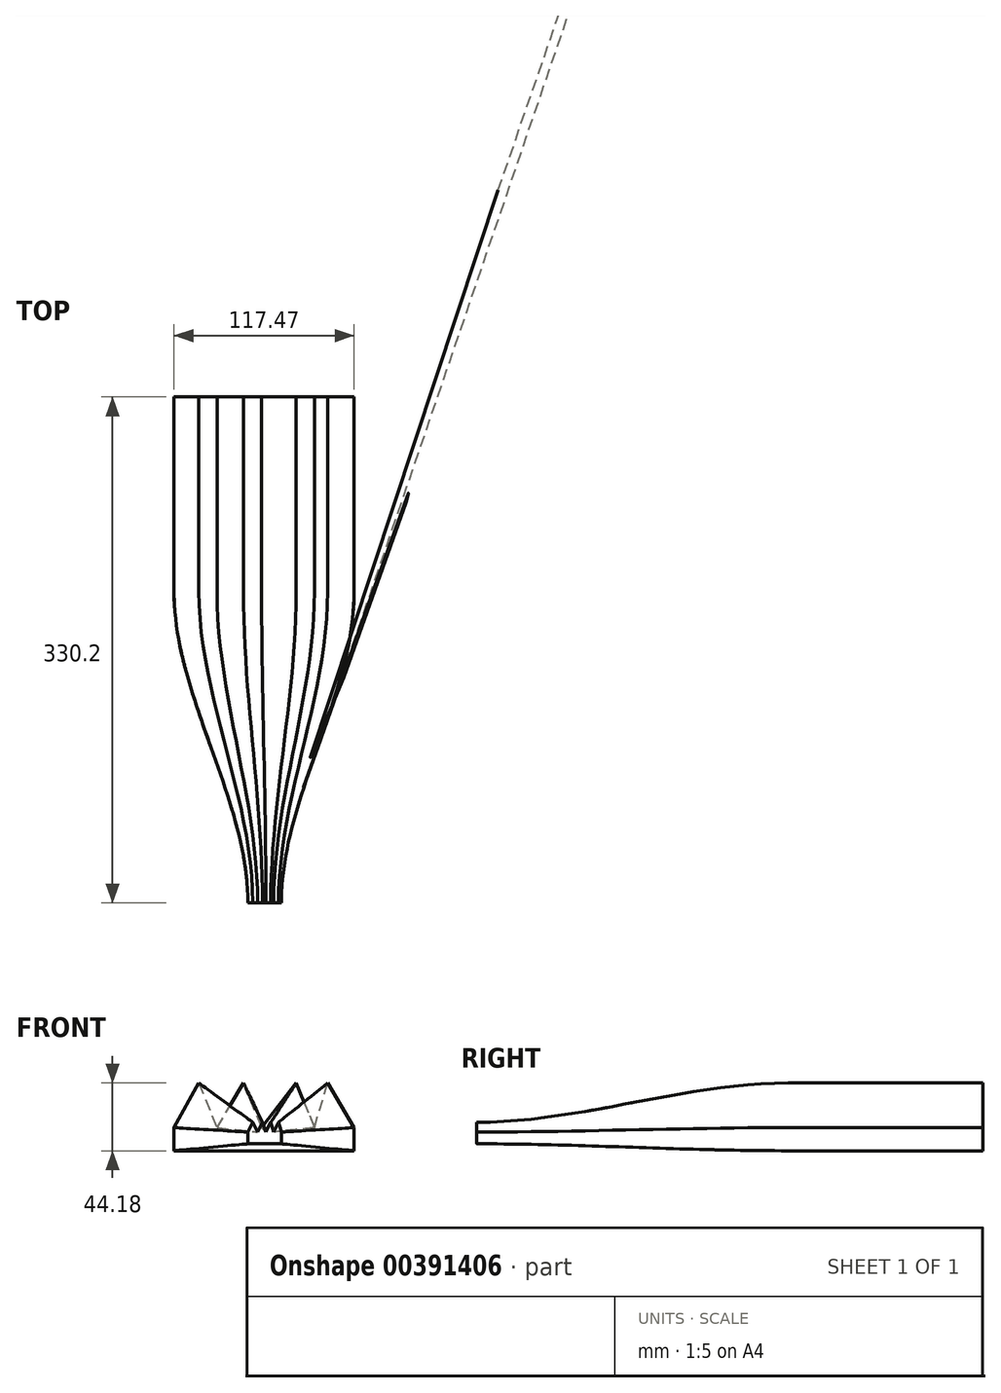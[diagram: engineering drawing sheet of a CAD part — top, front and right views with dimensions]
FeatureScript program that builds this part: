
annotation { "Feature Type Name" : "Feature", "Feature Type Description" : "" }
export const myFeature = defineFeature(function(context is Context, id is Id, definition is map)
    precondition{}
    {
        {
            var Q0;
            Q0=qCreatedBy(makeId("Front.planeOp"),FACE);
            var sketch = newSketch(context, id + "F0", { "sketchPlane" : qUnion([Q0])});
            skLineSegment(sketch, "E0.bottom", {"start": v(-57.12, 6.47) * mm, "end": v(60.35, 6.47) * mm});
            skLineSegment(sketch, "E0.top", {"start": v(-57.12, -8.62) * mm, "end": v(60.35, -8.62) * mm});
            skLineSegment(sketch, "E0.left", {"start": v(-57.12, 6.47) * mm, "end": v(-57.12, -8.62) * mm});
            skLineSegment(sketch, "E0.right", {"start": v(60.35, 6.47) * mm, "end": v(60.35, -8.62) * mm});
            skLineSegment(sketch, "E1", {"start": v(-57.12, 6.47) * mm, "end": v(-40.95, 35.56) * mm});
            skLineSegment(sketch, "E2", {"start": v(-40.95, 35.56) * mm, "end": v(-29.1, 6.47) * mm});
            skLineSegment(sketch, "E3", {"start": v(-29.1, 6.47) * mm, "end": v(-11.85, 35.56) * mm});
            skLineSegment(sketch, "E4", {"start": v(-11.85, 35.56) * mm, "end": v(0, 6.47) * mm});
            skLineSegment(sketch, "E5", {"start": v(0, 6.47) * mm, "end": v(22.63, 35.56) * mm});
            skLineSegment(sketch, "E6", {"start": v(22.63, 35.56) * mm, "end": v(34.49, 6.47) * mm});
            skLineSegment(sketch, "E7", {"start": v(34.49, 6.47) * mm, "end": v(43.1, 35.56) * mm});
            skLineSegment(sketch, "E8", {"start": v(43.1, 35.56) * mm, "end": v(60.35, 6.47) * mm});
            skSolve(sketch);
        }
        {
            var Q0;
            {var subQ0=sQuery(id+"F0.wireOp",EDGE,"E1");Q0=makeQuery(id+"F0.imprint","IMPRINT",FACE,{"disambiguationData":[TD([[makeQuery(id+"F0.imprint","IMPRINT",EDGE,{"derivedFrom":subQ0}),-1.0]])]});}
            var Q1;
            {var subQ0=sQuery(id+"F0.wireOp",EDGE,"E3");Q1=makeQuery(id+"F0.imprint","IMPRINT",FACE,{"disambiguationData":[TD([[makeQuery(id+"F0.imprint","IMPRINT",EDGE,{"derivedFrom":subQ0}),-1.0]])]});}
            var Q2;
            {var subQ0=sQuery(id+"F0.wireOp",EDGE,"E5");Q2=makeQuery(id+"F0.imprint","IMPRINT",FACE,{"disambiguationData":[TD([[makeQuery(id+"F0.imprint","IMPRINT",EDGE,{"derivedFrom":subQ0}),-1.0]])]});}
            var Q3;
            {var subQ2=sQuery(id+"F0.wireOp",EDGE,"E7");Q3=makeQuery(id+"F0.imprint","IMPRINT",FACE,{"disambiguationData":[TD([[makeQuery(id+"F0.imprint","IMPRINT",EDGE,{"derivedFrom":subQ2}),-1.0]])]});}
            var Q4;
            Q4=makeQuery(id+"F0.imprint","IMPRINT",FACE,{"disambiguationData":[TD([[makeQuery(id+"F0.imprint","IMPRINT",EDGE,{"derivedFrom":sQuery(id+"F0.wireOp",EDGE,"E0.top")}),1.0]])]});
            extrude(context, id + "F1", {"entities" : qUnion([Q0, Q1, Q2, Q3, Q4]), "depth" : 127 * mm});
        }
        {
            var Q0;
            Q0=makeQuery(id+"F1.opExtrude","CAP_FACE",FACE,{"disambiguationData":[OSD([sQuery(id+"F0.wireOp",EDGE,"E0.top"),sQuery(id+"F0.wireOp",EDGE,"E0.left"),sQuery(id+"F0.wireOp",EDGE,"E0.right"),sQuery(id+"F0.wireOp",EDGE,"E1"),sQuery(id+"F0.wireOp",EDGE,"E2"),sQuery(id+"F0.wireOp",EDGE,"E3"),sQuery(id+"F0.wireOp",EDGE,"E4"),sQuery(id+"F0.wireOp",EDGE,"E5"),sQuery(id+"F0.wireOp",EDGE,"E6"),sQuery(id+"F0.wireOp",EDGE,"E7"),sQuery(id+"F0.wireOp",EDGE,"E8")])],"isStart":false});
            cPlane(context, id + "F2", {"entities" : qUnion([Q0]), "cplaneType" : CPlaneType.OFFSET, "offset" : 203.2 * mm, "width" : 152.4 * mm, "height" : 152.4 * mm});
        }
        {
            var Q0;
            Q0=qCreatedBy(id+"F2.planeOp",FACE);
            var sketch = newSketch(context, id + "F3", { "sketchPlane" : qUnion([Q0])});
            skLineSegment(sketch, "E9.bottom", {"start": v(-8.92, 3.6) * mm, "end": v(12.83, 3.6) * mm});
            skLineSegment(sketch, "E9.top", {"start": v(-8.92, -4.1) * mm, "end": v(12.83, -4.1) * mm});
            skLineSegment(sketch, "E9.left", {"start": v(-8.92, 3.6) * mm, "end": v(-8.92, -4.1) * mm});
            skLineSegment(sketch, "E9.right", {"start": v(12.83, 3.6) * mm, "end": v(12.83, -4.1) * mm});
            skLineSegment(sketch, "E10", {"start": v(-8.92, 3.6) * mm, "end": v(-5.75, 9.94) * mm});
            skLineSegment(sketch, "E11", {"start": v(-5.75, 9.94) * mm, "end": v(-2.58, 3.6) * mm});
            skLineSegment(sketch, "E12", {"start": v(-2.58, 3.6) * mm, "end": v(0.6, 9.94) * mm});
            skLineSegment(sketch, "E13", {"start": v(0.6, 9.94) * mm, "end": v(2.86, 3.6) * mm});
            skLineSegment(sketch, "E14", {"start": v(2.86, 3.6) * mm, "end": v(6.03, 9.94) * mm});
            skLineSegment(sketch, "E15", {"start": v(6.03, 9.94) * mm, "end": v(7.84, 3.6) * mm});
            skLineSegment(sketch, "E16", {"start": v(7.84, 3.6) * mm, "end": v(11.02, 9.94) * mm});
            skLineSegment(sketch, "E17", {"start": v(11.02, 9.94) * mm, "end": v(12.83, 3.6) * mm});
            skSolve(sketch);
        }
        {
            var Q1;
            Q1=makeQuery(id+"F1.opExtrude","CAP_FACE",FACE,{"disambiguationData":[OSD([sQuery(id+"F0.wireOp",EDGE,"E0.top"),sQuery(id+"F0.wireOp",EDGE,"E0.left"),sQuery(id+"F0.wireOp",EDGE,"E0.right"),sQuery(id+"F0.wireOp",EDGE,"E1"),sQuery(id+"F0.wireOp",EDGE,"E2"),sQuery(id+"F0.wireOp",EDGE,"E3"),sQuery(id+"F0.wireOp",EDGE,"E4"),sQuery(id+"F0.wireOp",EDGE,"E5"),sQuery(id+"F0.wireOp",EDGE,"E6"),sQuery(id+"F0.wireOp",EDGE,"E7"),sQuery(id+"F0.wireOp",EDGE,"E8")])],"isStart":false});
            var Q2;
            Q2 = qSketchRegion(id + "F3", true);
            loft(context, id + "F4", {"operationType" : NewBodyOperationType.ADD, "startCondition" : LoftEndDerivativeType.NORMAL_TO_PROFILE, "startMagnitude" : 1, "endCondition" : LoftEndDerivativeType.NORMAL_TO_PROFILE, "endMagnitude" : 1, "sheetProfilesArray" : [{ "sheetProfileEntities" : qUnion([Q1]) }, { "sheetProfileEntities" : qUnion([Q2]) }]});
        }
    });
